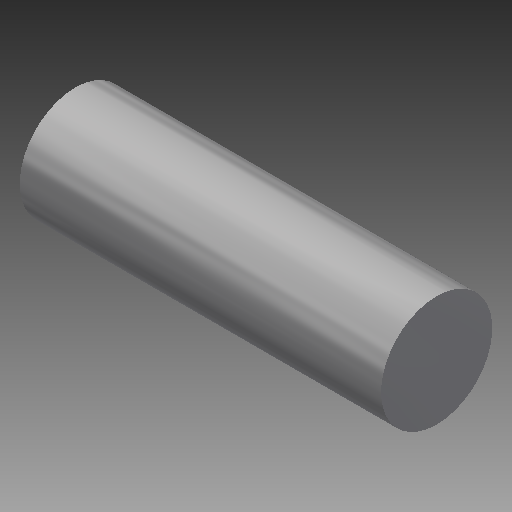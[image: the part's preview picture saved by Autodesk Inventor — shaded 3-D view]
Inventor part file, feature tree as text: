
AUTODESK INVENTOR PART (.ipt)
format: ipt  version: 2017 SP1 (Build 210196100, 196)  size: 104,960 bytes
history: native  units: mm
features: other x3, revolve x1
ambient origin geometry x6: Origin, XZ Plane, XY Plane, X Axis, Y Axis, Z Axis
bodies: Solid1 (feature_tree)
feature tree (4):
  revolve  "Revolution1"  [1 undecoded]
  other  "Start Plane"
  other  "Origin point"
  other  "Main Sketch"
note: 1 required parameter value undecoded (feature->parameter linkage not recoverable at this tier; creation-order binding heuristic only, values carry confidence <= 0.55)
